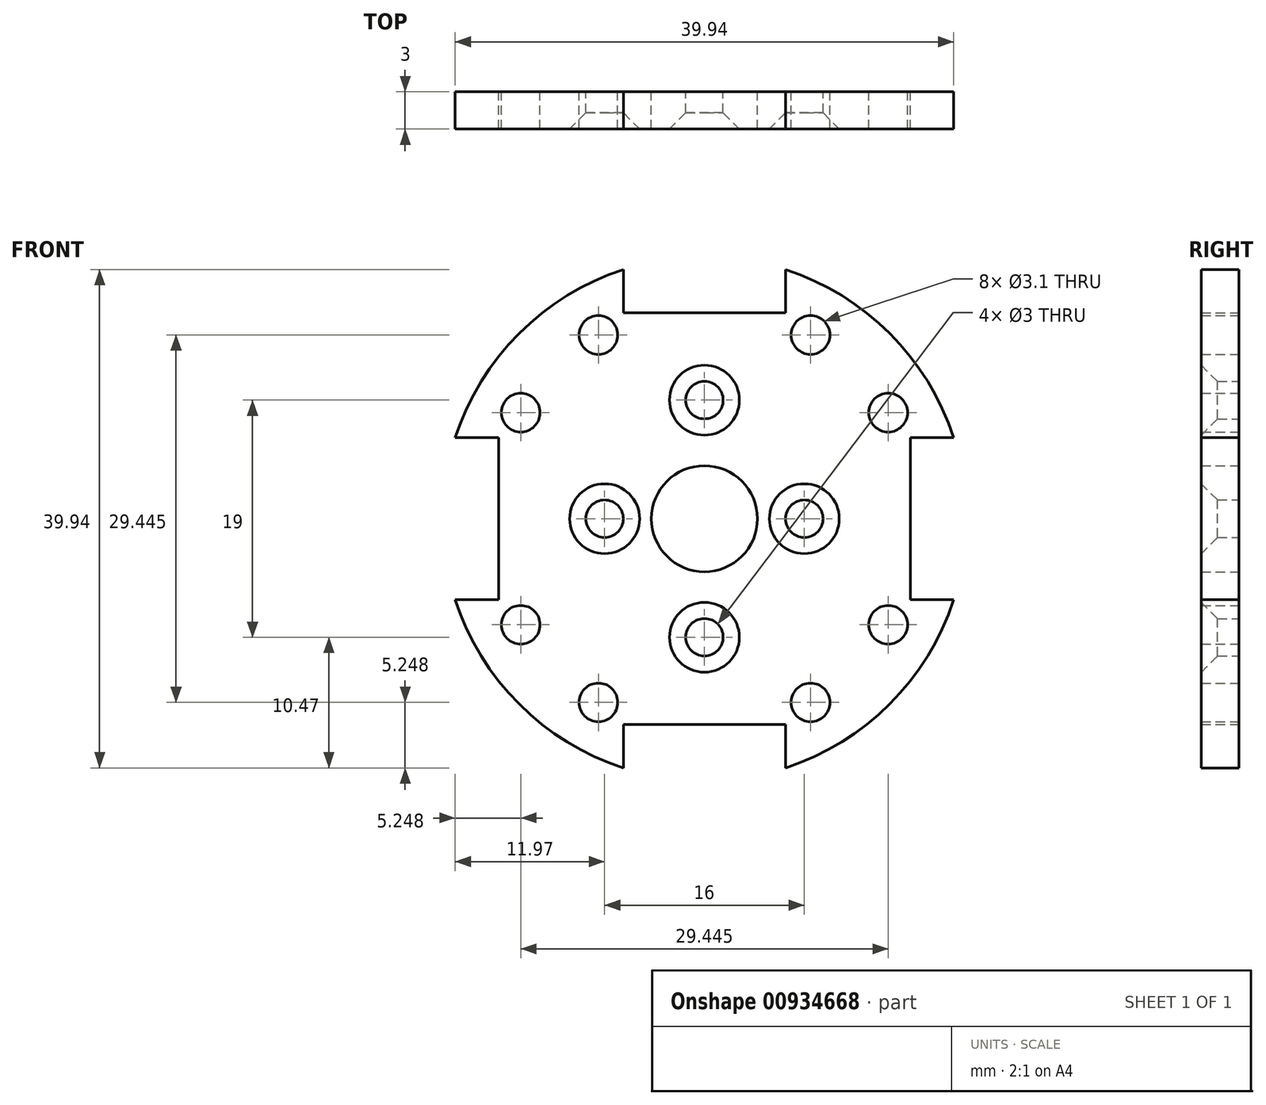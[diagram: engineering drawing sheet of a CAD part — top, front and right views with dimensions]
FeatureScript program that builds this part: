
annotation { "Feature Type Name" : "Feature", "Feature Type Description" : "" }
export const myFeature = defineFeature(function(context is Context, id is Id, definition is map)
    precondition{}
    {
        {
            var Q0;
            Q0=qCreatedBy(makeId("Front.planeOp"),FACE);
            var sketch = newSketch(context, id + "F0", { "sketchPlane" : qUnion([Q0])});
            skCircle(sketch, "E0", {"center": v(0, 0) * mm, "radius": 17 * mm, "construction": true});
            skArc(sketch, "E1", {"start": v(-19.97, -6.5) * mm, "mid": v(-14.85, -14.85) * mm, "end": v(-6.5, -19.97) * mm});
            skLineSegment(sketch, "E2", {"start": v(-19.97, 6.5) * mm, "end": v(-16.5, 6.5) * mm});
            skLineSegment(sketch, "E3", {"start": v(-16.5, 6.5) * mm, "end": v(-16.5, 0) * mm});
            skLineSegment(sketch, "E4.MirrorCS", {"start": v(-16.5, 13) * mm, "end": v(-16.5, 13) * mm});
            skLineSegment(sketch, "E5.MirrorCS", {"start": v(-19.97, -6.5) * mm, "end": v(-16.5, -6.5) * mm});
            skLineSegment(sketch, "E6.MirrorCS", {"start": v(-16.5, -6.5) * mm, "end": v(-16.5, 0) * mm});
            skLineSegment(sketch, "E7.1.0", {"start": v(-6.5, -19.97) * mm, "end": v(-6.5, -16.5) * mm});
            skLineSegment(sketch, "E7.1.1", {"start": v(-6.5, -16.5) * mm, "end": v(0, -16.5) * mm});
            skLineSegment(sketch, "E7.1.2", {"start": v(6.5, -16.5) * mm, "end": v(0, -16.5) * mm});
            skLineSegment(sketch, "E7.1.3", {"start": v(6.5, -19.97) * mm, "end": v(6.5, -16.5) * mm});
            skLineSegment(sketch, "E7.2.0", {"start": v(19.97, -6.5) * mm, "end": v(16.5, -6.5) * mm});
            skLineSegment(sketch, "E7.2.1", {"start": v(16.5, -6.5) * mm, "end": v(16.5, 0) * mm});
            skLineSegment(sketch, "E7.2.2", {"start": v(16.5, 6.5) * mm, "end": v(16.5, 0) * mm});
            skLineSegment(sketch, "E7.2.3", {"start": v(19.97, 6.5) * mm, "end": v(16.5, 6.5) * mm});
            skLineSegment(sketch, "E7.3.0", {"start": v(6.5, 19.97) * mm, "end": v(6.5, 16.5) * mm});
            skLineSegment(sketch, "E7.3.1", {"start": v(6.5, 16.5) * mm, "end": v(0, 16.5) * mm});
            skLineSegment(sketch, "E7.3.2", {"start": v(-6.5, 16.5) * mm, "end": v(0, 16.5) * mm});
            skLineSegment(sketch, "E7.3.3", {"start": v(-6.5, 19.97) * mm, "end": v(-6.5, 16.5) * mm});
            skArc(sketch, "E8.trimOffspring", {"start": v(-6.5, 19.97) * mm, "mid": v(-14.85, 14.85) * mm, "end": v(-19.97, 6.5) * mm});
            skArc(sketch, "E9.trimOffspring", {"start": v(19.97, 6.5) * mm, "mid": v(14.85, 14.85) * mm, "end": v(6.5, 19.97) * mm});
            skArc(sketch, "E10.trimOffspring", {"start": v(6.5, -19.97) * mm, "mid": v(14.85, -14.85) * mm, "end": v(19.97, -6.5) * mm});
            skLineSegment(sketch, "E11", {"start": v(-13, -22.5) * mm, "end": v(0, 0) * mm, "construction": true});
            skLineSegment(sketch, "E12", {"start": v(0, 0) * mm, "end": v(-25.73, -14.86) * mm, "construction": true});
            skCircle(sketch, "E13", {"center": v(-14.72, -8.5) * mm, "radius": 1.55 * mm});
            skCircle(sketch, "E14", {"center": v(-8.5, -14.72) * mm, "radius": 1.55 * mm});
            skCircle(sketch, "E15.1.0", {"center": v(8.5, -14.72) * mm, "radius": 1.55 * mm});
            skCircle(sketch, "E15.1.1", {"center": v(14.72, -8.5) * mm, "radius": 1.55 * mm});
            skCircle(sketch, "E15.2.0", {"center": v(14.72, 8.5) * mm, "radius": 1.55 * mm});
            skCircle(sketch, "E15.2.1", {"center": v(8.5, 14.72) * mm, "radius": 1.55 * mm});
            skCircle(sketch, "E15.3.0", {"center": v(-8.5, 14.72) * mm, "radius": 1.55 * mm});
            skCircle(sketch, "E15.3.1", {"center": v(-14.72, 8.5) * mm, "radius": 1.55 * mm});
            skCircle(sketch, "E16", {"center": v(8, 0) * mm, "radius": 1.5 * mm});
            skCircle(sketch, "E17", {"center": v(-8, 0) * mm, "radius": 1.5 * mm});
            skCircle(sketch, "E18", {"center": v(0, 9.5) * mm, "radius": 1.5 * mm});
            skCircle(sketch, "E19", {"center": v(0, -9.5) * mm, "radius": 1.5 * mm});
            skPoint(sketch, "E20.orphan", {"position": v(-16.5, 6.5) * mm});
            skCircle(sketch, "E21", {"center": v(0, 0) * mm, "radius": 4.25 * mm});
            skSolve(sketch);
        }
        {
            var Q0;
            Q0=makeQuery(id+"F0.imprint","IMPRINT",FACE,{"disambiguationData":[TD([[makeQuery(id+"F0.imprint","IMPRINT",EDGE,{"derivedFrom":sQuery(id+"F0.wireOp",EDGE,"E1")}),1.0]])]});
            extrude(context, id + "F1", {"entities" : qUnion([Q0]), "depth" : 3 * mm, "offsetDistance" : 25 * mm});
        }
        {
            var Q0;
            Q0=makeQuery(id+"F1.opExtrude","CAP_EDGE",EDGE,{"disambiguationData":[OSD([sQuery(id+"F0.wireOp",EDGE,"E18")])],"isStart":false});
            var Q1;
            Q1=makeQuery(id+"F1.opExtrude","CAP_EDGE",EDGE,{"disambiguationData":[OSD([sQuery(id+"F0.wireOp",EDGE,"E17")])],"isStart":false});
            var Q2;
            Q2=makeQuery(id+"F1.opExtrude","CAP_EDGE",EDGE,{"disambiguationData":[OSD([sQuery(id+"F0.wireOp",EDGE,"E16")])],"isStart":false});
            var Q3;
            Q3=makeQuery(id+"F1.opExtrude","CAP_EDGE",EDGE,{"disambiguationData":[OSD([sQuery(id+"F0.wireOp",EDGE,"E19")])],"isStart":false});
            chamfer(context, id + "F2", {"entities" : qUnion([Q0, Q1, Q2, Q3]), "width" : 1.3 * mm, "tangentPropagation" : true});
        }
    });
